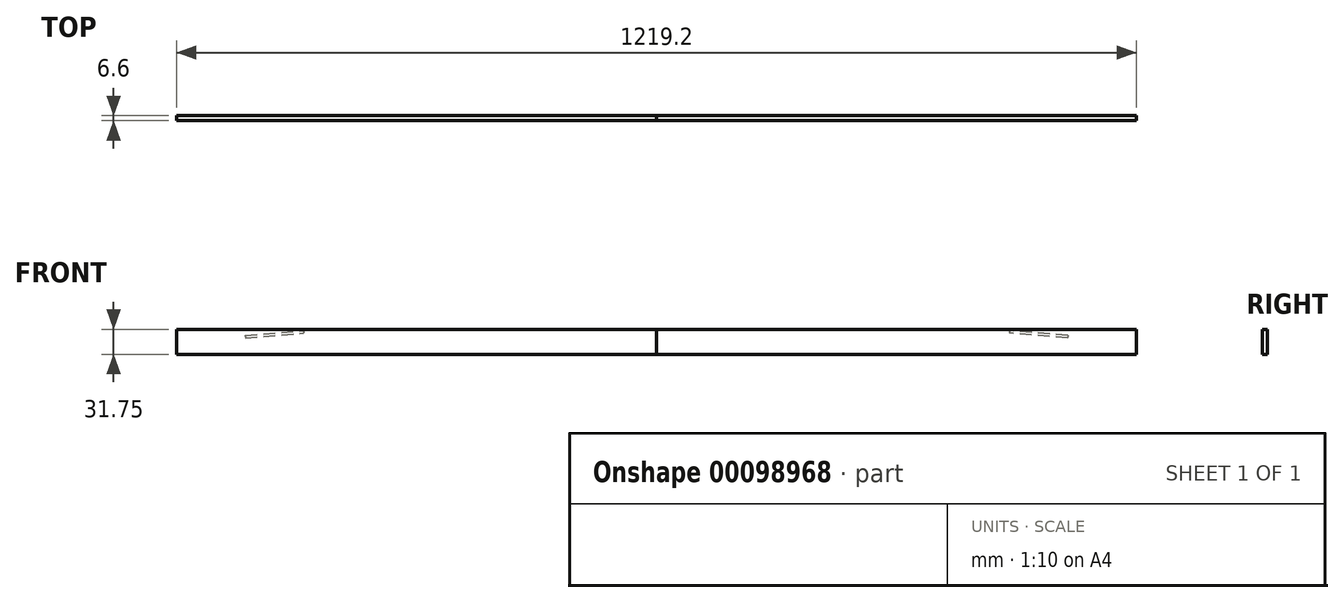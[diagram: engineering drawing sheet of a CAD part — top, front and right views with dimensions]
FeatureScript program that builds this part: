
annotation { "Feature Type Name" : "Feature", "Feature Type Description" : "" }
export const myFeature = defineFeature(function(context is Context, id is Id, definition is map)
    precondition{}
    {
        {
            var Q0;
            Q0=qCreatedBy(makeId("Front.planeOp"),FACE);
            var sketch = newSketch(context, id + "F0", { "sketchPlane" : qUnion([Q0])});
            skLineSegment(sketch, "E0.top", {"start": v(212.23, 24.52) * mm, "end": v(-397.37, 24.52) * mm});
            skLineSegment(sketch, "E1", {"start": v(-29.56, 22.94) * mm, "end": v(-29.28, 19.77) * mm});
            skLineSegment(sketch, "E2.0", {"start": v(-103.37, 16.48) * mm, "end": v(-103.1, 13.31) * mm});
            skLineSegment(sketch, "E3.0", {"start": v(-103.1, 13.31) * mm, "end": v(-29.28, 19.77) * mm});
            skLineSegment(sketch, "E4.0", {"start": v(-103.37, 16.48) * mm, "end": v(-29.56, 22.94) * mm});
            skLineSegment(sketch, "E5.MirrorCS", {"start": v(51.18, 22.94) * mm, "end": v(50.9, 19.77) * mm});
            skLineSegment(sketch, "E6.MirrorCS", {"start": v(125, 16.48) * mm, "end": v(51.18, 22.94) * mm});
            skLineSegment(sketch, "E7.MirrorCS", {"start": v(124.72, 13.31) * mm, "end": v(50.9, 19.77) * mm});
            skLineSegment(sketch, "E8.MirrorCS", {"start": v(125, 16.48) * mm, "end": v(124.72, 13.31) * mm});
            skLineSegment(sketch, "E9.0", {"start": v(-397.37, 24.52) * mm, "end": v(-397.37, -7.23) * mm});
            skLineSegment(sketch, "E10.0", {"start": v(212.23, 24.52) * mm, "end": v(212.23, -7.23) * mm});
            skLineSegment(sketch, "E11.trimOffspring", {"start": v(212.23, -7.23) * mm, "end": v(-397.37, -7.23) * mm});
            skSolve(sketch);
        }
        {
            var Q0;
            Q0=makeQuery(id+"F0.imprint","IMPRINT",FACE,{"disambiguationData":[TD([[makeQuery(id+"F0.imprint","IMPRINT",EDGE,{"derivedFrom":sQuery(id+"F0.wireOp",EDGE,"E0.top")}),1.0]])]});
            var Q1;
            Q1=makeQuery(id+"F0.imprint","IMPRINT",FACE,{"disambiguationData":[TD([[makeQuery(id+"F0.imprint","IMPRINT",EDGE,{"derivedFrom":sQuery(id+"F0.wireOp",EDGE,"E1")}),-1.0]])]});
            var Q2;
            Q2=makeQuery(id+"F0.imprint","IMPRINT",FACE,{"disambiguationData":[TD([[makeQuery(id+"F0.imprint","IMPRINT",EDGE,{"derivedFrom":sQuery(id+"F0.wireOp",EDGE,"E5.MirrorCS")}),1.0]])]});
            extrude(context, id + "F1", {"entities" : qUnion([Q0, Q1, Q2]), "depth" : 6.35 * mm});
        }
        {
            var Q0;
            Q0=makeQuery(id+"F1.opExtrude","SWEPT_BODY",BODY,{"disambiguationData":[OSD([sQuery(id+"F0.wireOp",EDGE,"E0.bottom"),sQuery(id+"F0.wireOp",EDGE,"E0.top"),sQuery(id+"F0.wireOp",EDGE,"E0.left"),sQuery(id+"F0.wireOp",EDGE,"E0.right")])]});
            var Q1;
            Q1=makeQuery(id+"F1.opExtrude","SWEPT_FACE",FACE,{"disambiguationData":[OSD([sQuery(id+"F0.wireOp",EDGE,"E9.0")])]});
            mirror(context, id + "F2", {"entities" : qUnion([Q0]), "mirrorPlane" : qUnion([Q1])});
        }
        {
            var Q0;
            Q0=makeQuery(id+"F0.imprint","IMPRINT",FACE,{"disambiguationData":[TD([[makeQuery(id+"F0.imprint","IMPRINT",EDGE,{"derivedFrom":sQuery(id+"F0.wireOp",EDGE,"E5.MirrorCS")}),1.0]])]});
            extrude(context, id + "F3", {"entities" : qUnion([Q0]), "operationType" : NewBodyOperationType.ADD, "oppositeDirection" : true, "depth" : 0.25 * mm});
        }
        {
            var Q0;
            Q0=makeQuery(id+"F2.opPattern","COPY",BODY,{"derivedFrom":makeQuery(id+"F1.opExtrude","SWEPT_BODY",BODY,{"disambiguationData":[OSD([sQuery(id+"F0.wireOp",EDGE,"E0.top"),sQuery(id+"F0.wireOp",EDGE,"E9.0"),sQuery(id+"F0.wireOp",EDGE,"E10.0"),sQuery(id+"F0.wireOp",EDGE,"E11.trimOffspring")])]}),"instanceName":"1"});
            deleteBodies(context, id + "F4", {"entities" : qUnion([Q0])});
        }
        {
            var Q0;
            Q0=makeQuery(id+"F1.opExtrude","SWEPT_BODY",BODY,{"disambiguationData":[OSD([sQuery(id+"F0.wireOp",EDGE,"E0.top"),sQuery(id+"F0.wireOp",EDGE,"E9.0"),sQuery(id+"F0.wireOp",EDGE,"E10.0"),sQuery(id+"F0.wireOp",EDGE,"E11.trimOffspring")])]});
            var Q1;
            Q1=makeQuery(id+"F1.opExtrude","SWEPT_FACE",FACE,{"disambiguationData":[OSD([sQuery(id+"F0.wireOp",EDGE,"E9.0")])]});
            mirror(context, id + "F5", {"entities" : qUnion([Q0]), "mirrorPlane" : qUnion([Q1])});
        }
    });
